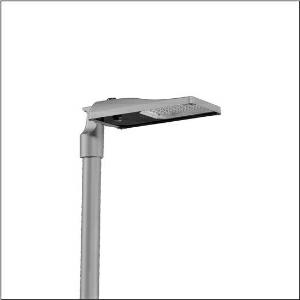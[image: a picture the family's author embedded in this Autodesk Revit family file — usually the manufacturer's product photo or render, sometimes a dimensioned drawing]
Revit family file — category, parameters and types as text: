
# Revit family: streetlight_sl_31_mini___st1_0a_5xh2d31t08ja_3c6a
name_source: partatom
category: Lighting Fixtures
units: mm (PartAtom-declared; Revit-internal decimal feet)

## family parameters
Cut with Voids When Loaded = No
Host = Face
Light Source = No
Part Type = Normal
Room Calculation Point = No
Round Connector Dimension = Use Diameter
Shared = No

## types (1)
- --- (1 x LED, 12270 lm, 82.5 W, 3000K)
    Apparent Load = 83 VA
    CIE Flux Codes = 40 73 97 100 100
    Color Rendering = 70
    Color Temperature = 3000K
    Default Elevation = 1800 mm
    Description = Streetlight SL 31 mini D4i, Desk-Remote mast luminaire for post-top, side-entry; light control with lens of PMMA; light distribution: ST1.0a, direct asymmetric distribution, for standard-compliant lighting for roads and squares; LED: luminous flux: 12.270lm, light colour: 730, colour temperature: 3000K; luminous efficacy: 148,7lm/W; control: pre-setting: logarithmic dimming characteristic, flexible luminous flux parameterisation, time-dependent luminous flux control, constant luminous flux control, power reduction, intelligent temperature release in ECG and LED module, overheat protection; luminaire housing, of diecast aluminium, SITECO metallic grey (DB 702S), corrosivity category C5 high according to DIN EN ISO 12944; cover of toughened safety glass, transparent, mast flange of diecast aluminium, SITECO metallic grey (DB 702S), spigot size: 76/60mm, mast flange included unmounted; with cable H07RN-F 2x 1.5mm², cable length: 10,5m, connection cable pre-assembled; mains connection: 220..240V, AC, 50/60Hz; power consumption (at start of service life): 82,5W / (at end of service life): 90,1W / (with reduced operation 50%): 36,8W; protection rating (complete): IP66; insulation class (complete): insulation class II (safety insulation); impact resistance: IK09; certification: CE, ENEC, ENEC+, VDE, UKCA, ZD4i; permissible operating ambient temperature for outdoor applications: -40..+50°C; packaging unit: 1 piece

Light Distribution: ST1.0a
    Height = 76 mm
    Lamp = 1 x LED
    Lamp Light Flux = 12270 lm
    Lamp Power = 82.5 W
    Lamp count = 1
    Length = 547 mm
    Luminous efficacy = 149 lm/W
    Manufacturer = Siteco
    ModVariant = No
    Model = 5XH2D31T08JA
    Number of Poles = 1
    OnlyDefault = Yes
    Power Factor = 1
    Product Name = Streetlight SL 31 mini | ST1.0a
    Product group = mast luminaire | pylon top
    ProductGroupID = 6100
    Protection Class = Protection class II
    Protection Degree = IP 66
    RLX_Detail_Level = 1
    RLX_Emergency_Light_Flux = 0 lm
    RLX_Emergency_Type = 0
    RLX_Emergency_Type_DB = No
    RlxData = <blob elided: 39873 chars, md5=08a38ac6>
    Socket = socket
    Standby Power = 0 W
    System Light Flux = 12270 lm
    System Power = 83 W
    Type Comments = factory setting: luminous flux: 100 % | dim-lin: 254 | 870 mA
    Type Image = l_1300332.jpg
    URL = http://relux.com
    VarID = @adj_057635
    Voltage = 0 V
    Weight = 0.00 kg
    Width = 265 mm

## geometry (parser evidence)
native form markers: Blend x4, Sweep x10
no freeform markers — native parametric forms only
